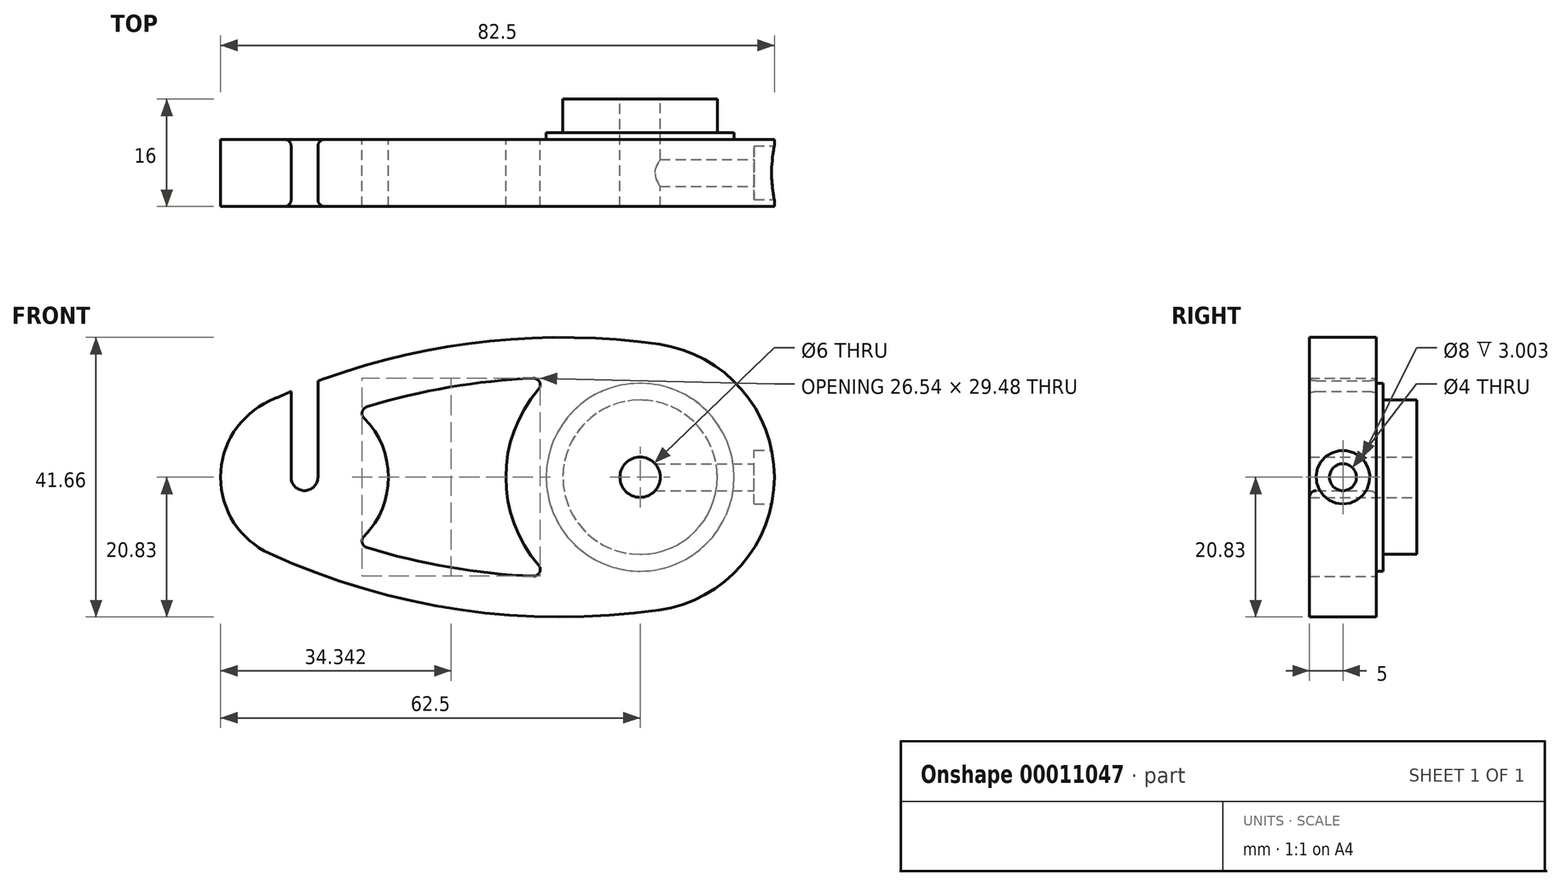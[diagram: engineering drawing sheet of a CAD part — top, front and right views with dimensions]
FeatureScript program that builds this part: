
annotation { "Feature Type Name" : "Feature", "Feature Type Description" : "" }
export const myFeature = defineFeature(function(context is Context, id is Id, definition is map)
    precondition{}
    {
        {
            var Q0;
            Q0=qCreatedBy(makeId("Front.planeOp"),FACE);
            var sketch = newSketch(context, id + "F0", { "sketchPlane" : qUnion([Q0])});
            skLineSegment(sketch, "E0", {"start": v(0, 0) * mm, "end": v(-50, 0) * mm, "construction": true});
            skArc(sketch, "E1", {"start": v(2.8, 19.8) * mm, "mid": v(-26.8, 19.74) * mm, "end": v(-55.2, 11.37) * mm});
            skLineSegment(sketch, "E2", {"start": v(-55.2, 11.37) * mm, "end": v(-55.2, -11.37) * mm, "construction": true});
            skLineSegment(sketch, "E3", {"start": v(2.8, 19.8) * mm, "end": v(2.8, -19.8) * mm, "construction": true});
            skArc(sketch, "E4", {"start": v(-55.2, -11.37) * mm, "mid": v(-26.8, -19.74) * mm, "end": v(2.8, -19.8) * mm});
            skArc(sketch, "E5", {"start": v(-55.2, 11.37) * mm, "mid": v(-62.5, 0) * mm, "end": v(-55.2, -11.37) * mm});
            skArc(sketch, "E6", {"start": v(-55.2, -11.37) * mm, "mid": v(-48.61, -12.42) * mm, "end": v(-42.42, -9.94) * mm, "construction": true});
            skArc(sketch, "E7", {"start": v(2.8, -19.8) * mm, "mid": v(20, 0) * mm, "end": v(2.8, 19.8) * mm});
            skArc(sketch, "E8", {"start": v(2.8, 19.8) * mm, "mid": v(-5.87, 19.12) * mm, "end": v(-13.44, 14.82) * mm, "construction": true});
            skArc(sketch, "E9.0", {"start": v(-13.44, 14.82) * mm, "mid": v(-28.1, 13.47) * mm, "end": v(-42.42, 9.94) * mm});
            skArc(sketch, "E10.0.MirrorCS", {"start": v(-13.44, -14.82) * mm, "mid": v(-28.1, -13.47) * mm, "end": v(-42.42, -9.94) * mm});
            skArc(sketch, "E11", {"start": v(-13.44, 14.82) * mm, "mid": v(-20, 0) * mm, "end": v(-13.44, -14.82) * mm});
            skArc(sketch, "E12", {"start": v(-13.44, -14.82) * mm, "mid": v(-5.87, -19.12) * mm, "end": v(2.8, -19.8) * mm, "construction": true});
            skArc(sketch, "E13", {"start": v(-42.42, 9.94) * mm, "mid": v(-48.61, 12.42) * mm, "end": v(-55.2, 11.37) * mm, "construction": true});
            skArc(sketch, "E14", {"start": v(-42.42, -9.94) * mm, "mid": v(-37.5, 0) * mm, "end": v(-42.42, 9.94) * mm});
            skCircle(sketch, "E15", {"center": v(0, 0) * mm, "radius": 3 * mm});
            skCircle(sketch, "E16", {"center": v(-50, 0) * mm, "radius": 2 * mm});
            skLineSegment(sketch, "E17", {"start": v(-52, 0) * mm, "end": v(-52, 12.77) * mm});
            skLineSegment(sketch, "E18", {"start": v(-48, 0) * mm, "end": v(-48, 14.34) * mm});
            skSolve(sketch);
        }
        {
            var Q0;
            Q0=makeQuery(id+"F0.imprint","IMPRINT",FACE,{"disambiguationData":[TD([[makeQuery(id+"F0.imprint","IMPRINT",EDGE,{"derivedFrom":sQuery(id+"F0.wireOp",EDGE,"E1")}),1.0]])]});
            extrude(context, id + "F1", {"entities" : qUnion([Q0]), "endBound" : BoundingType.SYMMETRIC, "depth" : 10 * mm});
        }
        {
            var Q0;
            Q0=makeQuery(id+"F1.opExtrude","CAP_EDGE",EDGE,{"disambiguationData":[OSD([sQuery(id+"F0.wireOp",EDGE,"E16")])],"isStart":false});
            var Q1;
            Q1=makeQuery(id+"F1.opExtrude","CAP_EDGE",EDGE,{"disambiguationData":[OSD([sQuery(id+"F0.wireOp",EDGE,"E16")])],"isStart":true});
            fillet(context, id + "F2", {"entities" : qUnion([Q0, Q1]), "radius" : 1 * mm, "tangentPropagation" : true, "allowEdgeOverflow" : false});
        }
        {
            var Q0;
            Q0=qCreatedBy(makeId("Right.planeOp"),FACE);
            cPlane(context, id + "F3", {"entities" : qUnion([Q0]), "cplaneType" : CPlaneType.OFFSET, "offset" : 20 * mm, "width" : 150 * mm, "height" : 150 * mm});
        }
        {
            var Q0;
            Q0=qCreatedBy(id+"F3.planeOp",FACE);
            var sketch = newSketch(context, id + "F4", { "sketchPlane" : qUnion([Q0])});
            skCircle(sketch, "E19", {"center": v(0, 0) * mm, "radius": 4 * mm});
            skCircle(sketch, "E20", {"center": v(0, 0) * mm, "radius": 2 * mm});
            skSolve(sketch);
        }
        {
            var Q0;
            Q0=makeQuery(id+"F4.imprint","IMPRINT",FACE,{"disambiguationData":[TD([[makeQuery(id+"F4.imprint","IMPRINT",EDGE,{"derivedFrom":sQuery(id+"F4.wireOp",EDGE,"E19")}),1.0]])]});
            var Q1;
            Q1=makeQuery(id+"F4.imprint","IMPRINT",FACE,{"disambiguationData":[TD([[makeQuery(id+"F4.imprint","IMPRINT",EDGE,{"derivedFrom":sQuery(id+"F4.wireOp",EDGE,"E20")}),1.0]])]});
            extrude(context, id + "F5", {"entities" : qUnion([Q0, Q1]), "operationType" : NewBodyOperationType.REMOVE, "oppositeDirection" : true, "depth" : 3 * mm});
        }
        {
            var Q0;
            Q0=makeQuery(id+"F4.imprint","IMPRINT",FACE,{"disambiguationData":[TD([[makeQuery(id+"F4.imprint","IMPRINT",EDGE,{"derivedFrom":sQuery(id+"F4.wireOp",EDGE,"E20")}),1.0]])]});
            var Q1;
            Q1=makeQuery(id+"F1.opExtrude","SWEPT_FACE",FACE,{"disambiguationData":[OSD([sQuery(id+"F0.wireOp",EDGE,"E15")])]});
            extrude(context, id + "F6", {"entities" : qUnion([Q0]), "operationType" : NewBodyOperationType.REMOVE, "endBound" : BoundingType.UP_TO_SURFACE, "oppositeDirection" : true, "endBoundEntityFace" : qUnion([Q1]), "depth" : 25 * mm});
        }
        {
            var Q0;
            Q0=makeQuery(id+"F1.opExtrude","CAP_FACE",FACE,{"disambiguationData":[OSD([sQuery(id+"F0.wireOp",EDGE,"E1"),sQuery(id+"F0.wireOp",EDGE,"E4"),sQuery(id+"F0.wireOp",EDGE,"E5"),sQuery(id+"F0.wireOp",EDGE,"E7"),sQuery(id+"F0.wireOp",EDGE,"E9.0"),sQuery(id+"F0.wireOp",EDGE,"E10.0.MirrorCS"),sQuery(id+"F0.wireOp",EDGE,"E11"),sQuery(id+"F0.wireOp",EDGE,"E14"),sQuery(id+"F0.wireOp",EDGE,"E15"),sQuery(id+"F0.wireOp",EDGE,"E16")])],"isStart":true});
            var sketch = newSketch(context, id + "F7", { "sketchPlane" : qUnion([Q0])});
            skCircle(sketch, "E21", {"center": v(0, 0) * mm, "radius": 11.5 * mm});
            skSolve(sketch);
        }
        {
            var Q0;
            Q0=makeQuery(id+"F7.imprint","IMPRINT",FACE,{"disambiguationData":[TD([[makeQuery(id+"F7.imprint","IMPRINT",EDGE,{"derivedFrom":sQuery(id+"F7.wireOp",EDGE,"E21")}),1.0]])]});
            extrude(context, id + "F8", {"entities" : qUnion([Q0]), "operationType" : NewBodyOperationType.ADD, "depth" : 6 * mm});
        }
        {
            var Q0;
            Q0=makeQuery(id+"F1.opExtrude","SWEPT_EDGE",EDGE,{"disambiguationData":[OSD([sQuery(id+"F0.wireOp",EDGE,"E9.0"),sQuery(id+"F0.wireOp",EDGE,"E14")])]});
            var Q1;
            Q1=makeQuery(id+"F1.opExtrude","SWEPT_EDGE",EDGE,{"disambiguationData":[OSD([sQuery(id+"F0.wireOp",EDGE,"E10.0.MirrorCS"),sQuery(id+"F0.wireOp",EDGE,"E14")])]});
            var Q2;
            Q2=makeQuery(id+"F1.opExtrude","SWEPT_EDGE",EDGE,{"disambiguationData":[OSD([sQuery(id+"F0.wireOp",EDGE,"E10.0.MirrorCS"),sQuery(id+"F0.wireOp",EDGE,"E11")])]});
            var Q3;
            Q3=makeQuery(id+"F1.opExtrude","SWEPT_EDGE",EDGE,{"disambiguationData":[OSD([sQuery(id+"F0.wireOp",EDGE,"E9.0"),sQuery(id+"F0.wireOp",EDGE,"E11")])]});
            fillet(context, id + "F9", {"entities" : qUnion([Q0, Q1, Q2, Q3]), "radius" : 1 * mm, "tangentPropagation" : true, "allowEdgeOverflow" : false});
        }
        {
            var Q0;
            Q0=makeQuery(id+"F1.opExtrude","CAP_FACE",FACE,{"disambiguationData":[OSD([sQuery(id+"F0.wireOp",EDGE,"E1"),sQuery(id+"F0.wireOp",EDGE,"E4"),sQuery(id+"F0.wireOp",EDGE,"E5"),sQuery(id+"F0.wireOp",EDGE,"E7"),sQuery(id+"F0.wireOp",EDGE,"E9.0"),sQuery(id+"F0.wireOp",EDGE,"E10.0.MirrorCS"),sQuery(id+"F0.wireOp",EDGE,"E11"),sQuery(id+"F0.wireOp",EDGE,"E14"),sQuery(id+"F0.wireOp",EDGE,"E15"),sQuery(id+"F0.wireOp",EDGE,"E16")])],"isStart":true});
            var sketch = newSketch(context, id + "F10", { "sketchPlane" : qUnion([Q0])});
            skCircle(sketch, "E22", {"center": v(0, 0) * mm, "radius": 14 * mm});
            skSolve(sketch);
        }
        {
            var Q0;
            Q0=makeQuery(id+"F10.imprint","IMPRINT",FACE,{"disambiguationData":[TD([[makeQuery(id+"F10.imprint","IMPRINT",EDGE,{"derivedFrom":sQuery(id+"F10.wireOp",EDGE,"E22")}),1.0]])]});
            extrude(context, id + "F11", {"entities" : qUnion([Q0]), "operationType" : NewBodyOperationType.ADD, "depth" : 1 * mm});
        }
    });
